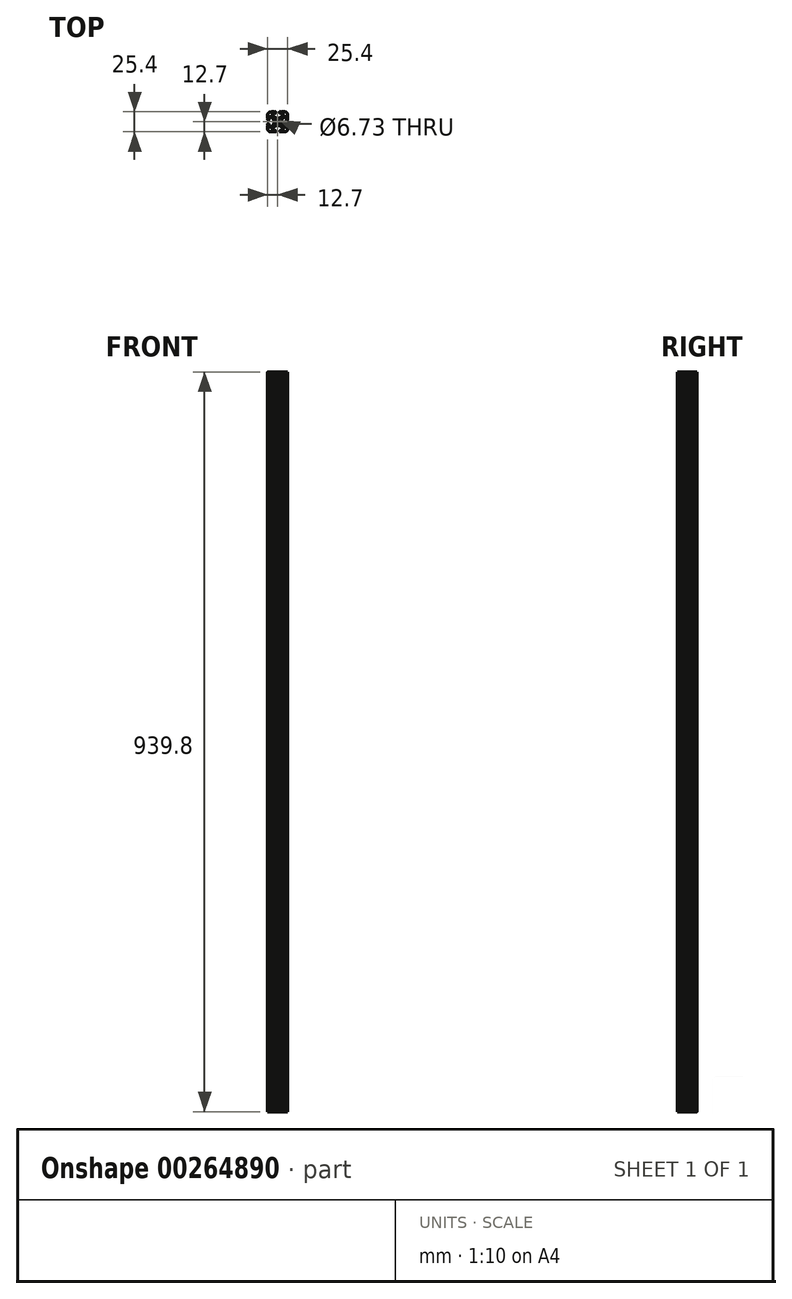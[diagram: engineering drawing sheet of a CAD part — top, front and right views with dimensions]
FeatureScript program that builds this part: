
annotation { "Feature Type Name" : "Feature", "Feature Type Description" : "" }
export const myFeature = defineFeature(function(context is Context, id is Id, definition is map)
    precondition{}
    {
        {
            var Q0;
            Q0=qCreatedBy(makeId("Top.planeOp"),FACE);
            var sketch = newSketch(context, id + "F0", { "sketchPlane" : qUnion([Q0])});
            skCircle(sketch, "E0", {"center": v(-12.7, 12.7) * mm, "radius": 3.36 * mm});
            skLineSegment(sketch, "E1.bottom", {"start": v(-11.24, 17.64) * mm, "end": v(-14.16, 17.64) * mm});
            skLineSegment(sketch, "E1.top", {"start": v(-11.24, 7.76) * mm, "end": v(-14.16, 7.76) * mm});
            skLineSegment(sketch, "E1.left", {"start": v(-7.76, 14.16) * mm, "end": v(-7.76, 11.24) * mm});
            skLineSegment(sketch, "E1.right", {"start": v(-17.64, 14.16) * mm, "end": v(-17.64, 11.24) * mm});
            skPoint(sketch, "E2.visualSharp", {"position": v(-25.4, 25.4) * mm});
            skPoint(sketch, "E3.visualSharp", {"position": v(0, 25.4) * mm});
            skPoint(sketch, "E4.visualSharp", {"position": v(0, 0) * mm});
            skPoint(sketch, "E5.visualSharp", {"position": v(-25.4, 0) * mm});
            skLineSegment(sketch, "E6.0", {"start": v(-18.7, 20.6) * mm, "end": v(-16.85, 18.76) * mm});
            skLineSegment(sketch, "E7.0", {"start": v(-20.6, 18.7) * mm, "end": v(-18.76, 16.85) * mm});
            skPoint(sketch, "E8.orphan", {"position": v(-23.85, 1.55) * mm});
            skPoint(sketch, "E9.orphan", {"position": v(-23.85, 23.85) * mm});
            skPoint(sketch, "E10.orphan", {"position": v(-1.55, 23.85) * mm});
            skPoint(sketch, "E11.orphan", {"position": v(-1.55, 1.55) * mm});
            skLineSegment(sketch, "E12", {"start": v(-8.55, 6.64) * mm, "end": v(-6.7, 4.8) * mm});
            skLineSegment(sketch, "E13.0", {"start": v(-18.7, 4.8) * mm, "end": v(-16.85, 6.64) * mm});
            skLineSegment(sketch, "E14.0", {"start": v(-20.6, 6.7) * mm, "end": v(-18.76, 8.55) * mm});
            skLineSegment(sketch, "E15.0", {"start": v(-8.55, 18.76) * mm, "end": v(-6.7, 20.6) * mm});
            skPoint(sketch, "E16.visualSharp", {"position": v(-23.85, 21.95) * mm});
            skArc(sketch, "E16.filletArc", {"start": v(-20.6, 18.7) * mm, "mid": v(-22.68, 19.1) * mm, "end": v(-23.85, 17.35) * mm});
            skPoint(sketch, "E17.visualSharp", {"position": v(-21.95, 23.85) * mm});
            skArc(sketch, "E17.filletArc", {"start": v(-17.35, 23.85) * mm, "mid": v(-19.1, 22.68) * mm, "end": v(-18.7, 20.6) * mm});
            skPoint(sketch, "E18.visualSharp", {"position": v(-5.34, 23.85) * mm});
            skLineSegment(sketch, "E19", {"start": v(-17.35, 23.85) * mm, "end": v(-15.58, 23.85) * mm});
            skLineSegment(sketch, "E20", {"start": v(-23.85, 17.35) * mm, "end": v(-23.85, 15.62) * mm});
            skLineSegment(sketch, "E21", {"start": v(-8.05, 1.55) * mm, "end": v(-9.78, 1.55) * mm});
            skArc(sketch, "E22.filletArc", {"start": v(-6.7, 20.6) * mm, "mid": v(-6.3, 22.68) * mm, "end": v(-8.05, 23.85) * mm});
            skPoint(sketch, "E23.visualSharp", {"position": v(-1.55, 3.45) * mm});
            skPoint(sketch, "E24.visualSharp", {"position": v(-3.45, 1.55) * mm});
            skArc(sketch, "E24.filletArc", {"start": v(-8.05, 1.55) * mm, "mid": v(-6.3, 2.73) * mm, "end": v(-6.7, 4.8) * mm});
            skArc(sketch, "E25.filletArc", {"start": v(-18.7, 4.8) * mm, "mid": v(-19.1, 2.73) * mm, "end": v(-17.35, 1.55) * mm});
            skArc(sketch, "E26.filletArc", {"start": v(-23.85, 8.05) * mm, "mid": v(-22.68, 6.3) * mm, "end": v(-20.6, 6.7) * mm});
            skLineSegment(sketch, "E27.bottom", {"start": v(-4.9, 0) * mm, "end": v(-8.05, 0) * mm});
            skLineSegment(sketch, "E27.top", {"start": v(-4.92, 25.4) * mm, "end": v(-8.05, 25.4) * mm});
            skLineSegment(sketch, "E27.left", {"start": v(0, 4.9) * mm, "end": v(0, 8.05) * mm});
            skLineSegment(sketch, "E27.right", {"start": v(-25.4, 4.9) * mm, "end": v(-25.4, 8.05) * mm});
            skArc(sketch, "E28.filletArc", {"start": v(-25.4, 3.81) * mm, "mid": v(-24.28, 1.12) * mm, "end": v(-21.59, 0) * mm});
            skArc(sketch, "E29.filletArc", {"start": v(-3.81, 0) * mm, "mid": v(-1.12, 1.12) * mm, "end": v(0, 3.8) * mm});
            skArc(sketch, "E30.filletArc", {"start": v(0, 21.59) * mm, "mid": v(-1.12, 24.28) * mm, "end": v(-3.8, 25.4) * mm});
            skArc(sketch, "E31.filletArc", {"start": v(-21.59, 25.4) * mm, "mid": v(-24.28, 24.28) * mm, "end": v(-25.4, 21.59) * mm});
            skPoint(sketch, "E32.newPointA", {"position": v(-17.64, 7.76) * mm});
            skArc(sketch, "E32.filletArc", {"start": v(-14.16, 7.76) * mm, "mid": v(-15.62, 7.47) * mm, "end": v(-16.85, 6.64) * mm});
            skPoint(sketch, "E33.newPointA", {"position": v(-7.76, 7.76) * mm});
            skArc(sketch, "E33.filletArc", {"start": v(-8.55, 6.64) * mm, "mid": v(-9.78, 7.47) * mm, "end": v(-11.24, 7.76) * mm});
            skArc(sketch, "E34.filletArc", {"start": v(-7.76, 11.24) * mm, "mid": v(-7.47, 9.78) * mm, "end": v(-6.64, 8.55) * mm});
            skArc(sketch, "E35.filletArc", {"start": v(-6.64, 16.85) * mm, "mid": v(-7.47, 15.62) * mm, "end": v(-7.76, 14.16) * mm});
            skPoint(sketch, "E36.newPointB", {"position": v(-7.76, 17.64) * mm});
            skArc(sketch, "E36.filletArc", {"start": v(-11.24, 17.64) * mm, "mid": v(-9.78, 17.93) * mm, "end": v(-8.55, 18.76) * mm});
            skPoint(sketch, "E37.newPointB", {"position": v(-17.64, 17.64) * mm});
            skArc(sketch, "E37.filletArc", {"start": v(-16.85, 18.76) * mm, "mid": v(-15.62, 17.93) * mm, "end": v(-14.16, 17.64) * mm});
            skArc(sketch, "E38.filletArc", {"start": v(-17.64, 14.16) * mm, "mid": v(-17.93, 15.62) * mm, "end": v(-18.76, 16.85) * mm});
            skArc(sketch, "E39.filletArc", {"start": v(-18.76, 8.55) * mm, "mid": v(-17.93, 9.78) * mm, "end": v(-17.64, 11.24) * mm});
            skLineSegment(sketch, "E40", {"start": v(-6.64, 8.55) * mm, "end": v(-4.8, 6.7) * mm});
            skPoint(sketch, "E41.visualSharp", {"position": v(-1.55, 21.95) * mm});
            skArc(sketch, "E42.filletArc", {"start": v(-4.8, 6.7) * mm, "mid": v(-2.73, 6.3) * mm, "end": v(-1.55, 8.05) * mm});
            skLineSegment(sketch, "E43", {"start": v(-1.55, 8.05) * mm, "end": v(-1.55, 9.78) * mm});
            skLineSegment(sketch, "E44", {"start": v(-6.64, 16.85) * mm, "end": v(-4.8, 18.7) * mm});
            skArc(sketch, "E45.filletArc", {"start": v(-1.55, 17.35) * mm, "mid": v(-2.73, 19.1) * mm, "end": v(-4.8, 18.7) * mm});
            skArc(sketch, "E46", {"start": v(-23.85, 9.78) * mm, "mid": v(-24.63, 10.56) * mm, "end": v(-25.4, 9.78) * mm});
            skArc(sketch, "E47", {"start": v(-25.4, 15.62) * mm, "mid": v(-24.63, 14.86) * mm, "end": v(-23.85, 15.62) * mm});
            skArc(sketch, "E48", {"start": v(-15.62, 23.85) * mm, "mid": v(-14.83, 24.63) * mm, "end": v(-15.62, 25.4) * mm});
            skArc(sketch, "E49", {"start": v(-9.78, 25.4) * mm, "mid": v(-10.6, 24.63) * mm, "end": v(-9.78, 23.85) * mm});
            skArc(sketch, "E50", {"start": v(-1.55, 15.62) * mm, "mid": v(-0.77, 14.88) * mm, "end": v(0, 15.62) * mm});
            skArc(sketch, "E51", {"start": v(0, 9.78) * mm, "mid": v(-0.77, 10.5) * mm, "end": v(-1.55, 9.78) * mm});
            skArc(sketch, "E52", {"start": v(-9.78, 1.55) * mm, "mid": v(-10.4, 0.77) * mm, "end": v(-9.78, 0) * mm});
            skArc(sketch, "E53", {"start": v(-15.62, 0) * mm, "mid": v(-14.85, 0.77) * mm, "end": v(-15.62, 1.55) * mm});
            skLineSegment(sketch, "E54.trimOffspring", {"start": v(-15.62, 1.55) * mm, "end": v(-17.35, 1.55) * mm});
            skLineSegment(sketch, "E55.trimOffspring", {"start": v(-16.7, 0) * mm, "end": v(-20.5, 0) * mm});
            skLineSegment(sketch, "E56.trimOffspring", {"start": v(-1.55, 15.62) * mm, "end": v(-1.55, 17.35) * mm});
            skLineSegment(sketch, "E57.trimOffspring", {"start": v(0, 15.62) * mm, "end": v(0, 16.26) * mm});
            skLineSegment(sketch, "E58.trimOffspring", {"start": v(-23.85, 9.78) * mm, "end": v(-23.85, 8.05) * mm});
            skLineSegment(sketch, "E59.trimOffspring", {"start": v(-25.4, 15.62) * mm, "end": v(-25.4, 16.26) * mm});
            skLineSegment(sketch, "E60.trimOffspring", {"start": v(-9.86, 23.85) * mm, "end": v(-8.05, 23.85) * mm});
            skLineSegment(sketch, "E61.trimOffspring", {"start": v(-15.58, 25.4) * mm, "end": v(-16.25, 25.4) * mm});
            skPoint(sketch, "E62.start.orphan", {"position": v(-15.62, 17.93) * mm});
            skPoint(sketch, "E63.start.orphan", {"position": v(-9.78, 17.93) * mm});
            skPoint(sketch, "E64.start.orphan", {"position": v(-7.47, 15.62) * mm});
            skPoint(sketch, "E65.start.orphan", {"position": v(-7.47, 9.78) * mm});
            skPoint(sketch, "E66.start.orphan", {"position": v(-17.93, 15.62) * mm});
            skPoint(sketch, "E67.start.orphan", {"position": v(-17.93, 9.78) * mm});
            skPoint(sketch, "E68.start.orphan", {"position": v(-9.78, 7.47) * mm});
            skPoint(sketch, "E69.start.orphan", {"position": v(-15.62, 7.47) * mm});
            skPoint(sketch, "E70.endSnap0", {"position": v(0, 18.6) * mm});
            skPoint(sketch, "E71.startSnap0", {"position": v(-1.55, 8.92) * mm});
            skArc(sketch, "E72", {"start": v(-4.92, 25.4) * mm, "mid": v(-4.37, 24.9) * mm, "end": v(-3.81, 25.4) * mm});
            skArc(sketch, "E73", {"start": v(-9.14, 25.4) * mm, "mid": v(-8.6, 24.86) * mm, "end": v(-8.05, 25.4) * mm});
            skArc(sketch, "E74", {"start": v(-17.35, 25.4) * mm, "mid": v(-16.8, 24.86) * mm, "end": v(-16.25, 25.4) * mm});
            skArc(sketch, "E75", {"start": v(-21.6, 25.4) * mm, "mid": v(-21.04, 24.85) * mm, "end": v(-20.49, 25.4) * mm});
            skLineSegment(sketch, "E76", {"start": v(-25.4, 21.59) * mm, "end": v(-25.4, 20.5) * mm});
            skArc(sketch, "E77", {"start": v(-25.4, 16.26) * mm, "mid": v(-24.84, 16.8) * mm, "end": v(-25.4, 17.35) * mm});
            skArc(sketch, "E78", {"start": v(-25.4, 8.05) * mm, "mid": v(-24.9, 8.6) * mm, "end": v(-25.4, 9.15) * mm});
            skArc(sketch, "E79", {"start": v(-25.4, 3.81) * mm, "mid": v(-24.85, 4.36) * mm, "end": v(-25.4, 4.9) * mm});
            skArc(sketch, "E80", {"start": v(-20.5, 0) * mm, "mid": v(-21.04, 0.55) * mm, "end": v(-21.59, 0) * mm});
            skArc(sketch, "E81", {"start": v(-15.62, 0) * mm, "mid": v(-16.16, 0.54) * mm, "end": v(-16.7, 0) * mm});
            skArc(sketch, "E82", {"start": v(-8.05, 0) * mm, "mid": v(-8.6, 0.55) * mm, "end": v(-9.15, 0) * mm});
            skArc(sketch, "E83", {"start": v(-3.81, 0) * mm, "mid": v(-4.35, 0.54) * mm, "end": v(-4.9, 0) * mm});
            skLineSegment(sketch, "E84.trimOffspring", {"start": v(-17.35, 25.4) * mm, "end": v(-20.49, 25.4) * mm});
            skLineSegment(sketch, "E85.trimOffspring", {"start": v(-25.4, 17.35) * mm, "end": v(-25.4, 21.59) * mm});
            skLineSegment(sketch, "E86.trimOffspring", {"start": v(-25.4, 9.15) * mm, "end": v(-25.4, 9.78) * mm});
            skLineSegment(sketch, "E87.trimOffspring", {"start": v(-9.15, 0) * mm, "end": v(-9.78, 0) * mm});
            skArc(sketch, "E88", {"start": v(0, 4.9) * mm, "mid": v(-0.54, 4.36) * mm, "end": v(0, 3.8) * mm});
            skArc(sketch, "E89", {"start": v(0, 9.15) * mm, "mid": v(-0.54, 8.6) * mm, "end": v(0, 8.05) * mm});
            skLineSegment(sketch, "E90.trimOffspring", {"start": v(0, 9.15) * mm, "end": v(0, 9.78) * mm});
            skArc(sketch, "E91", {"start": v(0, 21.59) * mm, "mid": v(-0.55, 21.04) * mm, "end": v(0, 20.5) * mm});
            skArc(sketch, "E92", {"start": v(0, 17.35) * mm, "mid": v(-0.55, 16.8) * mm, "end": v(0, 16.26) * mm});
            skLineSegment(sketch, "E93.trimOffspring", {"start": v(0, 17.35) * mm, "end": v(0, 20.5) * mm});
            skLineSegment(sketch, "E94.trimOffspring", {"start": v(-9.14, 25.4) * mm, "end": v(-9.86, 25.4) * mm});
            skSolve(sketch);
        }
        {
            var Q0;
            Q0=qSketchRegion(id+"F0",true);
            extrude(context, id + "F1", {"entities" : qUnion([Q0]), "depth" : 939.8 * mm});
        }
    });
